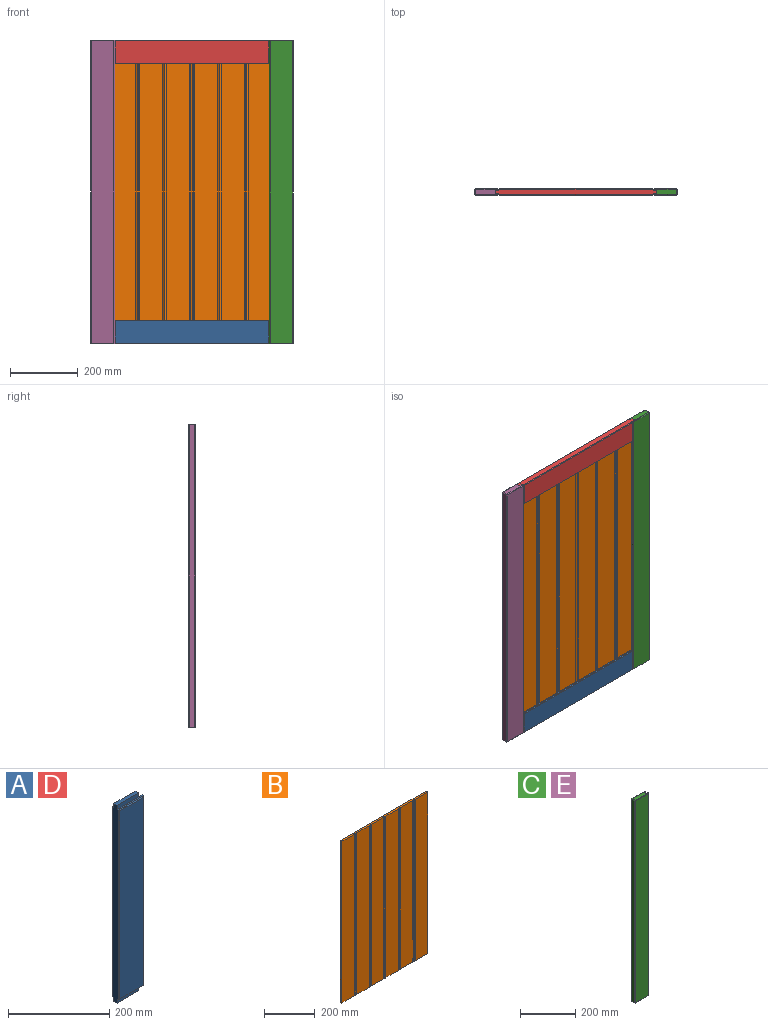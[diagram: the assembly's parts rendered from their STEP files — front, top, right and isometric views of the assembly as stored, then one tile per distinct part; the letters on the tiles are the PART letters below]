
ASSEMBLY  parts=5 mates=12
PART A: 26 faces, bbox 70x20x478 mm
  f0: plane 478x16mm, normal (-1,0,0), area 7508mm2, adj f7,f8,f10,f11,f12,f13,f14,f15
  f1: plane 454x66mm, normal (0,-1,0), area 29964mm2, adj f18,f19,f20,f21
  f2: plane 458x3.5mm, normal (1,0,0), area 1603mm2, adj f3,f10,f17,f21
  f3: plane 458x10mm, normal (0,1,0), area 4580mm2, adj f2,f9,f10,f17
  f4: plane 458x10mm, normal (0,-1,0), area 4580mm2, adj f5,f9,f12,f15
  f5: plane 458x3.5mm, normal (1,0,0), area 1603mm2, adj f4,f12,f15,f22
  f6: plane 454x66mm, normal (0,1,0), area 29964mm2, adj f22,f23,f24,f25
  f7: plane 60x9mm, normal (0,0,1), area 540mm2, adj f0,f9,f14,f16
  f8: plane 60x9mm, normal (0,0,-1), area 540mm2, adj f0,f9,f11,f13
  f9: plane 478x9mm, normal (1,0,0), area 4302mm2, adj f3,f4,f7,f8,f11,f13,f14,f16
  f10: plane 70x3.5mm, normal (0,0,-1), area 245mm2, adj f0,f2,f3,f11,f20
  f11: plane 60x10mm, normal (0,-1,0), area 600mm2, adj f0,f8,f9,f10
  f12: plane 70x3.5mm, normal (0,0,-1), area 245mm2, adj f0,f4,f5,f13,f24
  f13: plane 60x10mm, normal (0,1,0), area 600mm2, adj f0,f8,f9,f12
  f14: plane 60x10mm, normal (0,1,0), area 600mm2, adj f0,f7,f9,f15
  f15: plane 70x3.5mm, normal (0,0,1), area 245mm2, adj f0,f4,f5,f14,f23
  f16: plane 60x10mm, normal (0,-1,0), area 600mm2, adj f0,f7,f9,f17
  f17: plane 70x3.5mm, normal (0,0,1), area 245mm2, adj f0,f2,f3,f16,f19
  f18: plane 458x2mm, normal (-0.71,-0.71,0), area 1289.8mm2, adj f0,f1,f19,f20
  f19: plane 70x2mm, normal (0,-0.71,0.71), area 192.3mm2, adj f1,f17,f18,f21
  f20: plane 70x2mm, normal (0,-0.71,-0.71), area 192.3mm2, adj f1,f10,f18,f21
  f21: plane 458x2mm, normal (0.71,-0.71,0), area 1289.8mm2, adj f1,f2,f19,f20
  f22: plane 458x2mm, normal (0.71,0.71,0), area 1289.8mm2, adj f5,f6,f23,f24
  f23: plane 70x2mm, normal (0,0.71,0.71), area 192.3mm2, adj f6,f15,f22,f25
  f24: plane 70x2mm, normal (0,0.71,-0.71), area 192.3mm2, adj f6,f12,f22,f25
  f25: plane 458x2mm, normal (-0.71,0.71,0), area 1289.8mm2, adj f0,f6,f23,f24
PART B: 41 faces, bbox 478x9x778 mm
  f0: plane 478x9mm, normal (0,0,1), area 4256.6mm2, adj f1,f2,f3,f4,f5,f6,f8,f9
  f1: plane 778x71mm, normal (0,-1,0), area 55238mm2, adj f0,f6,f7,f29
  f2: plane 778x69mm, normal (0,-1,0), area 53682mm2, adj f0,f7,f25,f28
  f3: plane 778x69mm, normal (0,-1,0), area 53682mm2, adj f0,f7,f21,f24
  f4: plane 778x69mm, normal (0,-1,0), area 53682mm2, adj f0,f7,f17,f20
  f5: plane 778x69mm, normal (0,-1,0), area 53682mm2, adj f0,f7,f13,f16
  f6: plane 778x9mm, normal (-1,0,0), area 7002mm2, adj f0,f1,f7,f10
  f7: plane 478x9mm, normal (0,0,-1), area 4256.6mm2, adj f1,f2,f3,f4,f5,f6,f8,f9
  f8: plane 778x9mm, normal (1,0,0), area 7002mm2, adj f0,f7,f9,f10
  f9: plane 778x71mm, normal (0,-1,0), area 55238mm2, adj f0,f7,f8,f12
  f10: plane 778x478mm, normal (0,1,0), area 371884mm2, adj f0,f6,f7,f8
  f11: plane 778x0.54mm, normal (0.71,-0.71,0), area 589.2mm2, adj f0,f7,f12,f32
  f12: plane 778x2mm, normal (-0.71,-0.71,0), area 2200.5mm2, adj f0,f7,f9,f11
  f13: plane 778x2mm, normal (0.71,-0.71,0), area 2200.5mm2, adj f0,f5,f7,f14
  f14: plane 778x0.54mm, normal (-0.71,-0.71,0), area 589.2mm2, adj f0,f7,f13,f31
  f15: plane 778x0.54mm, normal (0.71,-0.71,0), area 589.2mm2, adj f0,f7,f16,f34
  f16: plane 778x2mm, normal (-0.71,-0.71,0), area 2200.5mm2, adj f0,f5,f7,f15
  f17: plane 778x2mm, normal (0.71,-0.71,0), area 2200.5mm2, adj f0,f4,f7,f18
  f18: plane 778x0.54mm, normal (-0.71,-0.71,0), area 589.2mm2, adj f0,f7,f17,f33
  f19: plane 778x0.54mm, normal (0.71,-0.71,0), area 589.2mm2, adj f0,f7,f20,f36
  f20: plane 778x2mm, normal (-0.71,-0.71,0), area 2200.5mm2, adj f0,f4,f7,f19
  f21: plane 778x2mm, normal (0.71,-0.71,0), area 2200.5mm2, adj f0,f3,f7,f22
  f22: plane 778x0.54mm, normal (-0.71,-0.71,0), area 589.2mm2, adj f0,f7,f21,f35
  f23: plane 778x0.54mm, normal (0.71,-0.71,0), area 589.2mm2, adj f0,f7,f24,f38
  f24: plane 778x2mm, normal (-0.71,-0.71,0), area 2200.5mm2, adj f0,f3,f7,f23
  f25: plane 778x2mm, normal (0.71,-0.71,0), area 2200.5mm2, adj f0,f2,f7,f26
  f26: plane 778x0.54mm, normal (-0.71,-0.71,0), area 589.2mm2, adj f0,f7,f25,f37
  f27: plane 778x0.54mm, normal (0.71,-0.71,0), area 589.2mm2, adj f0,f7,f28,f40
  f28: plane 778x2mm, normal (-0.71,-0.71,0), area 2200.5mm2, adj f0,f2,f7,f27
  f29: plane 778x2mm, normal (0.71,-0.71,0), area 2200.5mm2, adj f0,f1,f7,f30
  f30: plane 778x0.54mm, normal (-0.71,-0.71,0), area 589.2mm2, adj f0,f7,f29,f39
  f31: cylinder r=5mm len=778mm, axis (0,0,1), area 2999.9mm2, adj f0,f7,f14,f32
  f32: cylinder r=5mm len=778mm, axis (0,0,1), area 2999.9mm2, adj f0,f7,f11,f31
  f33: cylinder r=5mm len=778mm, axis (0,0,1), area 2999.9mm2, adj f0,f7,f18,f34
  f34: cylinder r=5mm len=778mm, axis (0,0,1), area 2999.9mm2, adj f0,f7,f15,f33
  f35: cylinder r=5mm len=778mm, axis (0,0,1), area 2999.9mm2, adj f0,f7,f22,f36
  f36: cylinder r=5mm len=778mm, axis (0,0,1), area 2999.9mm2, adj f0,f7,f19,f35
  f37: cylinder r=5mm len=778mm, axis (0,0,1), area 2999.9mm2, adj f0,f7,f26,f38
  f38: cylinder r=5mm len=778mm, axis (0,0,1), area 2999.9mm2, adj f0,f7,f23,f37
  f39: cylinder r=5mm len=778mm, axis (0,0,1), area 2999.9mm2, adj f0,f7,f30,f40
  f40: cylinder r=5mm len=778mm, axis (0,0,1), area 2999.9mm2, adj f0,f7,f27,f39
PART C: 24 faces, bbox 70x20x898 mm
  f0: plane 894x16mm, normal (-1,0,0), area 14304mm2, adj f13,f15,f18,f19
  f1: plane 894x66mm, normal (0,-1,0), area 59004mm2, adj f18,f20,f22,f23
  f2: plane 898x3.5mm, normal (1,0,0), area 3143mm2, adj f3,f8,f9,f22
  f3: plane 898x10mm, normal (0,1,0), area 8980mm2, adj f2,f4,f8,f9
  f4: plane 898x9mm, normal (1,0,0), area 8082mm2, adj f3,f5,f8,f9
  f5: plane 898x10mm, normal (0,-1,0), area 8980mm2, adj f4,f6,f8,f9
  f6: plane 898x3.5mm, normal (1,0,0), area 3143mm2, adj f5,f8,f9,f11
  f7: plane 894x66mm, normal (0,1,0), area 59004mm2, adj f10,f11,f13,f14
  f8: plane 68x16mm, normal (0,0,1), area 998mm2, adj f2,f3,f4,f5,f6,f14,f19,f23
  f9: plane 68x16mm, normal (0,0,-1), area 998mm2, adj f2,f3,f4,f5,f6,f10,f15,f20
  f10: plane 68x2mm, normal (0,0.71,-0.71), area 189.5mm2, adj f7,f9,f11,f12
  f11: plane 898x2mm, normal (0.71,0.71,0), area 2534.3mm2, adj f6,f7,f10,f14
  f12: plane 2x2mm, normal (-0.58,0.58,-0.58), area 3.5mm2, adj f10,f13,f15
  f13: plane 894x2mm, normal (-0.71,0.71,0), area 2528.6mm2, adj f0,f7,f12,f16
  f14: plane 68x2mm, normal (0,0.71,0.71), area 189.5mm2, adj f7,f8,f11,f16
  f15: plane 16x2mm, normal (-0.71,0,-0.71), area 45.3mm2, adj f0,f9,f12,f17
  f16: plane 2x2mm, normal (-0.58,0.58,0.58), area 3.5mm2, adj f13,f14,f19
  f17: plane 2x2mm, normal (-0.58,-0.58,-0.58), area 3.5mm2, adj f15,f18,f20
  f18: plane 894x2mm, normal (-0.71,-0.71,0), area 2528.6mm2, adj f0,f1,f17,f21
  f19: plane 16x2mm, normal (-0.71,0,0.71), area 45.3mm2, adj f0,f8,f16,f21
  f20: plane 68x2mm, normal (0,-0.71,-0.71), area 189.5mm2, adj f1,f9,f17,f22
  f21: plane 2x2mm, normal (-0.58,-0.58,0.58), area 3.5mm2, adj f18,f19,f23
  f22: plane 898x2mm, normal (0.71,-0.71,0), area 2534.3mm2, adj f1,f2,f20,f23
  f23: plane 68x2mm, normal (0,-0.71,0.71), area 189.5mm2, adj f1,f8,f21,f22
PART D: same geometry as A
PART E: same geometry as C
PLACE A rot(axis=(0,-1,0),90deg) t=(1020.13,-427.15,-1792.9)mm
PLACE B t=(542.13,-412.65,-1732.9)mm
PLACE C rot(axis=(0,0,1),180deg) t=(1080.13,-407.15,-1792.9)mm
PLACE D rot(axis=(0.71,0,-0.71),180deg) t=(1020.13,-407.15,-894.9)mm
PLACE E t=(482.13,-427.15,-1792.9)mm
MATE planar E.f1 <-> D.f6  axis (0,-1,0) through (517.13,-427.15,-1343.9)mm
MATE planar B.f7 <-> A.f9  axis (0,0,-1) through (781.13,-417.1,-1732.9)mm
MATE planar A.f1 <-> E.f1  axis (0,-1,0) through (781.13,-427.15,-1724.9)mm
MATE planar B.f6 <-> E.f4  axis (-1,0,0) through (542.13,-417.15,-1343.9)mm
MATE planar C.f8 <-> D.f0  axis (0,0,1) through (1046.75,-417.15,-894.9)mm
MATE planar A.f17 <-> E.f2  axis (-1,0,0) through (552.13,-423.4,-1757.9)mm
MATE planar D.f6 <-> C.f7  axis (0,-1,0) through (781.13,-427.15,-962.9)mm
MATE planar E.f5 <-> B.f10  axis (0,-1,0) through (547.13,-412.65,-1343.9)mm
MATE planar C.f2 <-> D.f10  axis (-1,0,0) through (1010.13,-410.9,-1343.9)mm
MATE planar E.f8 <-> D.f0  axis (0,0,1) through (515.52,-417.15,-894.9)mm
MATE planar D.f17 <-> E.f2  axis (-1,0,0) through (552.13,-410.9,-929.9)mm
MATE planar A.f0 <-> E.f9  axis (0,0,-1) through (781.13,-417.15,-1792.9)mm
